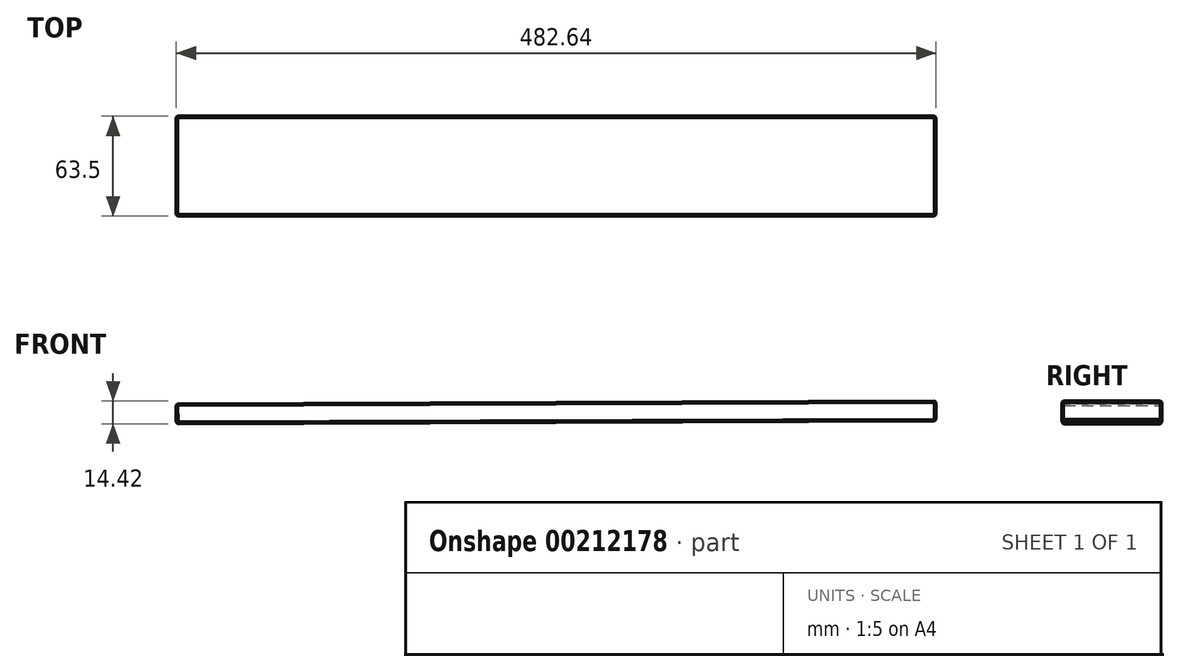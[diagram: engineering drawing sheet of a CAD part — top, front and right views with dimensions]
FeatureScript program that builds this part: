
annotation { "Feature Type Name" : "Feature", "Feature Type Description" : "" }
export const myFeature = defineFeature(function(context is Context, id is Id, definition is map)
    precondition{}
    {
        {
            var Q0;
            Q0=qCreatedBy(makeId("Front.planeOp"),FACE);
            var sketch = newSketch(context, id + "F0", { "sketchPlane" : qUnion([Q0])});
            skLineSegment(sketch, "E0", {"start": v(0, 0) * mm, "end": v(482.6, 1.73) * mm});
            skLineSegment(sketch, "E1", {"start": v(482.6, 1.73) * mm, "end": v(482.64, -10.97) * mm});
            skLineSegment(sketch, "E2", {"start": v(482.64, -10.97) * mm, "end": v(0.05, -12.7) * mm});
            skLineSegment(sketch, "E3", {"start": v(0, 0) * mm, "end": v(0.05, -12.7) * mm});
            skLineSegment(sketch, "E4", {"start": v(0, 0) * mm, "end": v(0, 114.92) * mm, "construction": true});
            skLineSegment(sketch, "E5", {"start": v(0, 39.83) * mm, "end": v(530.8, 39.83) * mm, "construction": true});
            skLineSegment(sketch, "E6", {"start": v(0, 0) * mm, "end": v(-101.6, 0) * mm, "construction": true});
            skLineSegment(sketch, "E7", {"start": v(-101.6, 0) * mm, "end": v(-101.6, 39.69) * mm, "construction": true});
            skSolve(sketch);
        }
        {
            var Q0;
            Q0=makeQuery(id+"F0.imprint","IMPRINT",FACE,{"disambiguationData":[TD([[makeQuery(id+"F0.imprint","IMPRINT",EDGE,{"derivedFrom":sQuery(id+"F0.wireOp",EDGE,"E0")}),-1.0]])]});
            extrude(context, id + "F1", {"entities" : qUnion([Q0]), "depth" : 63.5 * mm});
        }
        {
            var Q0;
            Q0=makeQuery(id+"F1.opExtrude","SWEPT_FACE",FACE,{"disambiguationData":[OSD([sQuery(id+"F0.wireOp",EDGE,"E0")])]});
            var Q1;
            Q1=makeQuery(id+"F1.opExtrude","SWEPT_FACE",FACE,{"disambiguationData":[OSD([sQuery(id+"F0.wireOp",EDGE,"E2")])]});
            var Q2;
            Q2=makeQuery(id+"F1.opExtrude","CAP_EDGE",EDGE,{"disambiguationData":[OSD([sQuery(id+"F0.wireOp",EDGE,"E1")])],"isStart":false});
            var Q3;
            Q3=makeQuery(id+"F1.opExtrude","CAP_EDGE",EDGE,{"disambiguationData":[OSD([sQuery(id+"F0.wireOp",EDGE,"E1")])],"isStart":true});
            var Q4;
            Q4=makeQuery(id+"F1.opExtrude","CAP_EDGE",EDGE,{"disambiguationData":[OSD([sQuery(id+"F0.wireOp",EDGE,"E3")])],"isStart":false});
            var Q5;
            Q5=makeQuery(id+"F1.opExtrude","CAP_EDGE",EDGE,{"disambiguationData":[OSD([sQuery(id+"F0.wireOp",EDGE,"E3")])],"isStart":true});
            chamfer(context, id + "F2", {"entities" : qUnion([Q0, Q1, Q2, Q3, Q4, Q5]), "width" : 1.02 * mm, "tangentPropagation" : true});
        }
    });
